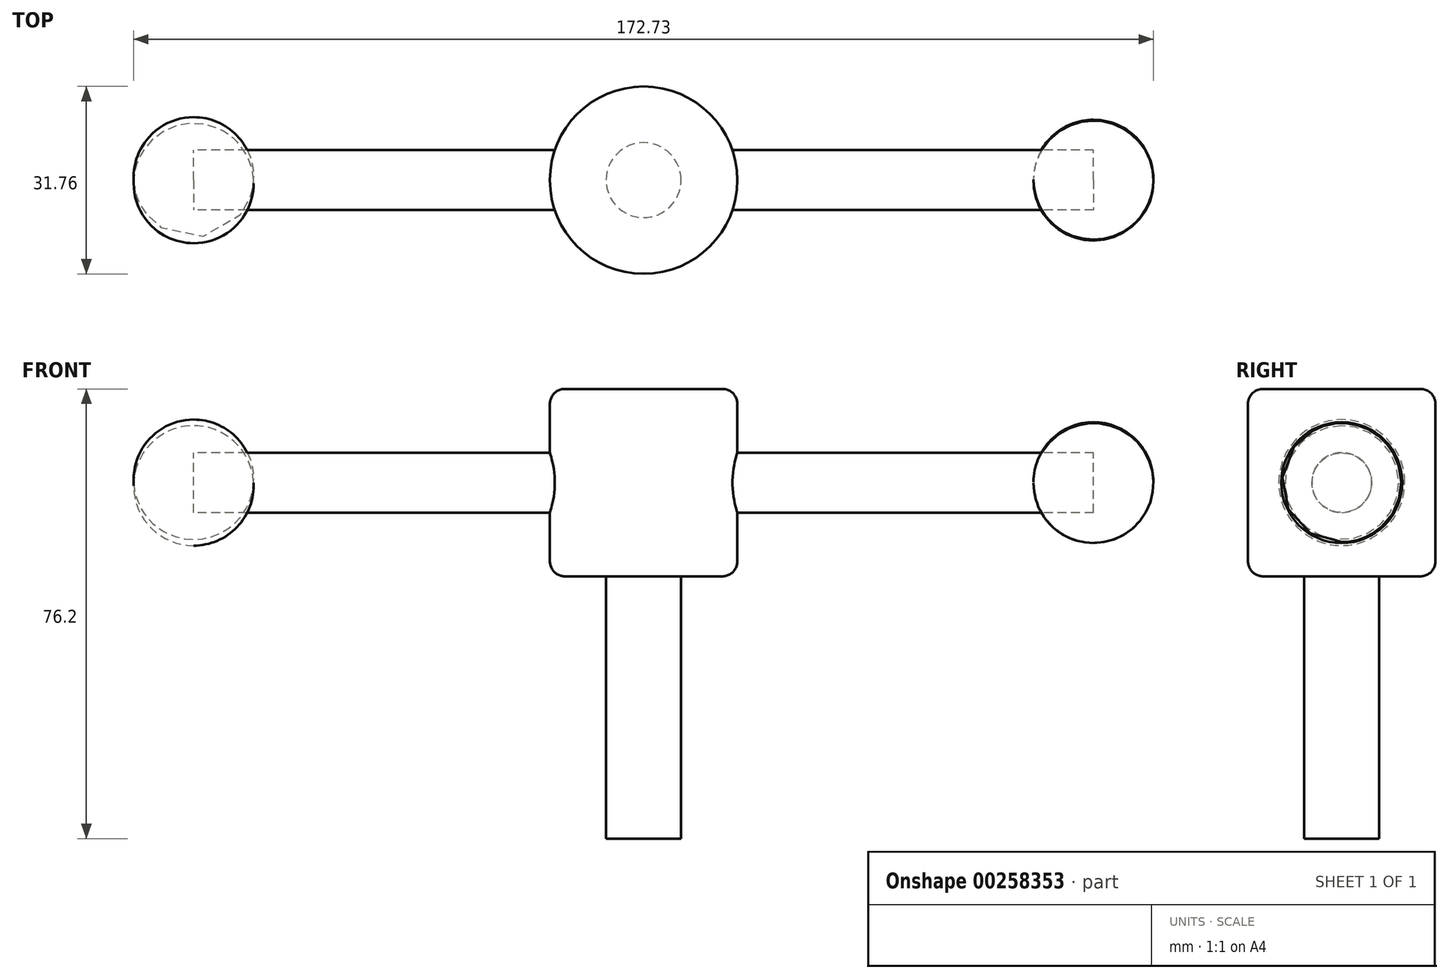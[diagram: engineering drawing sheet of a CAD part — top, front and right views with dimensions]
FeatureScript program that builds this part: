
annotation { "Feature Type Name" : "Feature", "Feature Type Description" : "" }
export const myFeature = defineFeature(function(context is Context, id is Id, definition is map)
    precondition{}
    {
        {
            var Q0;
            Q0=qCreatedBy(makeId("Top.planeOp"),FACE);
            var sketch = newSketch(context, id + "F0", { "sketchPlane" : qUnion([Q0])});
            skCircle(sketch, "E0", {"center": v(0, 0) * mm, "radius": 6.35 * mm});
            skSolve(sketch);
        }
        {
            var Q0;
            Q0=makeQuery(id+"F0.imprint","IMPRINT",FACE,{"disambiguationData":[TD([[makeQuery(id+"F0.imprint","IMPRINT",EDGE,{"derivedFrom":sQuery(id+"F0.wireOp",EDGE,"E0")}),1.0]])]});
            extrude(context, id + "F1", {"entities" : qUnion([Q0]), "depth" : 44.45 * mm});
        }
        {
            var Q0;
            Q0=makeQuery(id+"F1.opExtrude","CAP_FACE",FACE,{"disambiguationData":[OSD([sQuery(id+"F0.wireOp",EDGE,"E0")])],"isStart":false});
            var sketch = newSketch(context, id + "F2", { "sketchPlane" : qUnion([Q0])});
            skCircle(sketch, "E1", {"center": v(0, 0) * mm, "radius": 15.88 * mm});
            skSolve(sketch);
        }
        {
            var Q0;
            Q0=makeQuery(id+"F2.imprint","IMPRINT",FACE,{"disambiguationData":[TD([[makeQuery(id+"F2.imprint","IMPRINT",EDGE,{"derivedFrom":sQuery(id+"F2.wireOp",EDGE,"E1")}),1.0]])]});
            var Q1;
            Q1=makeQuery(id+"F2.imprint","IMPRINT",FACE,{"disambiguationData":[TD([[makeQuery(id+"F2.imprint","IMPRINT",EDGE,{"derivedFrom":makeQuery(id+"F1.opExtrude","CAP_EDGE",EDGE,{"disambiguationData":[OSD([sQuery(id+"F0.wireOp",EDGE,"E0")])],"isStart":false})}),1.0]])]});
            extrude(context, id + "F3", {"entities" : qUnion([Q0, Q1]), "operationType" : NewBodyOperationType.ADD, "depth" : 31.75 * mm});
        }
        {
            var Q0;
            Q0=makeQuery(id+"F3.opExtrude","CAP_EDGE",EDGE,{"disambiguationData":[OSD([sQuery(id+"F2.wireOp",EDGE,"E1")])],"isStart":false});
            var Q1;
            Q1=makeQuery(id+"F3.opExtrude","CAP_EDGE",EDGE,{"disambiguationData":[OSD([sQuery(id+"F2.wireOp",EDGE,"E1")])],"isStart":true});
            fillet(context, id + "F4", {"entities" : qUnion([Q0, Q1]), "radius" : 2.54 * mm, "tangentPropagation" : true, "allowEdgeOverflow" : false});
        }
        {
            var Q0;
            Q0=qCreatedBy(makeId("Right.planeOp"),FACE);
            var sketch = newSketch(context, id + "F5", { "sketchPlane" : qUnion([Q0])});
            skLineSegment(sketch, "E2", {"start": v(0, 0) * mm, "end": v(0, 60.33) * mm});
            skCircle(sketch, "E3", {"center": v(0, 60.33) * mm, "radius": 5.08 * mm});
            skSolve(sketch);
        }
        {
            var Q0;
            Q0=makeQuery(id+"F5.imprint","IMPRINT",FACE,{"disambiguationData":[TD([[makeQuery(id+"F5.imprint","IMPRINT",EDGE,{"derivedFrom":sQuery(id+"F5.wireOp",EDGE,"E3")}),1.0]])]});
            var Q1;
            Q1=sQuery(id+"F5.wireOp",EDGE,"E3");
            extrude(context, id + "F6", {"entities" : qUnion([Q0]), "operationType" : NewBodyOperationType.ADD, "surfaceEntities" : qUnion([Q1]), "endBound" : BoundingType.SYMMETRIC, "depth" : 152.4 * mm});
        }
        {
            var Q0;
            Q0=qCreatedBy(makeId("Front.planeOp"),FACE);
            var sketch = newSketch(context, id + "F7", { "sketchPlane" : qUnion([Q0])});
            skLineSegment(sketch, "E4", {"start": v(66.04, 60.32) * mm, "end": v(86.36, 60.32) * mm});
            skArc(sketch, "E5", {"start": v(86.36, 60.33) * mm, "mid": v(76.2, 70.4) * mm, "end": v(66.04, 60.32) * mm});
            skLineSegment(sketch, "E6", {"start": v(-66.07, 60.32) * mm, "end": v(-86.36, 60.32) * mm});
            skArc(sketch, "E7", {"start": v(-66.07, 60.32) * mm, "mid": v(-76.21, 69.97) * mm, "end": v(-86.36, 60.32) * mm});
            skSolve(sketch);
        }
        {
            var Q0;
            Q0=makeQuery(id+"F7.imprint","IMPRINT",FACE,{"disambiguationData":[TD([[makeQuery(id+"F7.imprint","IMPRINT",EDGE,{"derivedFrom":sQuery(id+"F7.wireOp",EDGE,"E4")}),1.0]])]});
            var Q1;
            Q1=sQuery(id+"F7.wireOp",EDGE,"E5");
            var Q2;
            Q2=sQuery(id+"F7.wireOp",EDGE,"E4");
            revolve(context, id + "F8", {"entities" : qUnion([Q0]), "surfaceEntities" : qUnion([Q1]), "axis" : qUnion([Q2]), "revolveType" : RevolveType.FULL});
        }
        {
            var Q0;
            Q0=makeQuery(id+"F7.imprint","IMPRINT",FACE,{"disambiguationData":[TD([[makeQuery(id+"F7.imprint","IMPRINT",EDGE,{"derivedFrom":sQuery(id+"F7.wireOp",EDGE,"E6")}),-1.0]])]});
            var Q1;
            Q1=sQuery(id+"F7.wireOp",EDGE,"E7");
            var Q2;
            Q2=sQuery(id+"F7.wireOp",EDGE,"E6");
            revolve(context, id + "F9", {"entities" : qUnion([Q0]), "surfaceEntities" : qUnion([Q1]), "axis" : qUnion([Q2]), "revolveType" : RevolveType.FULL});
        }
    });
